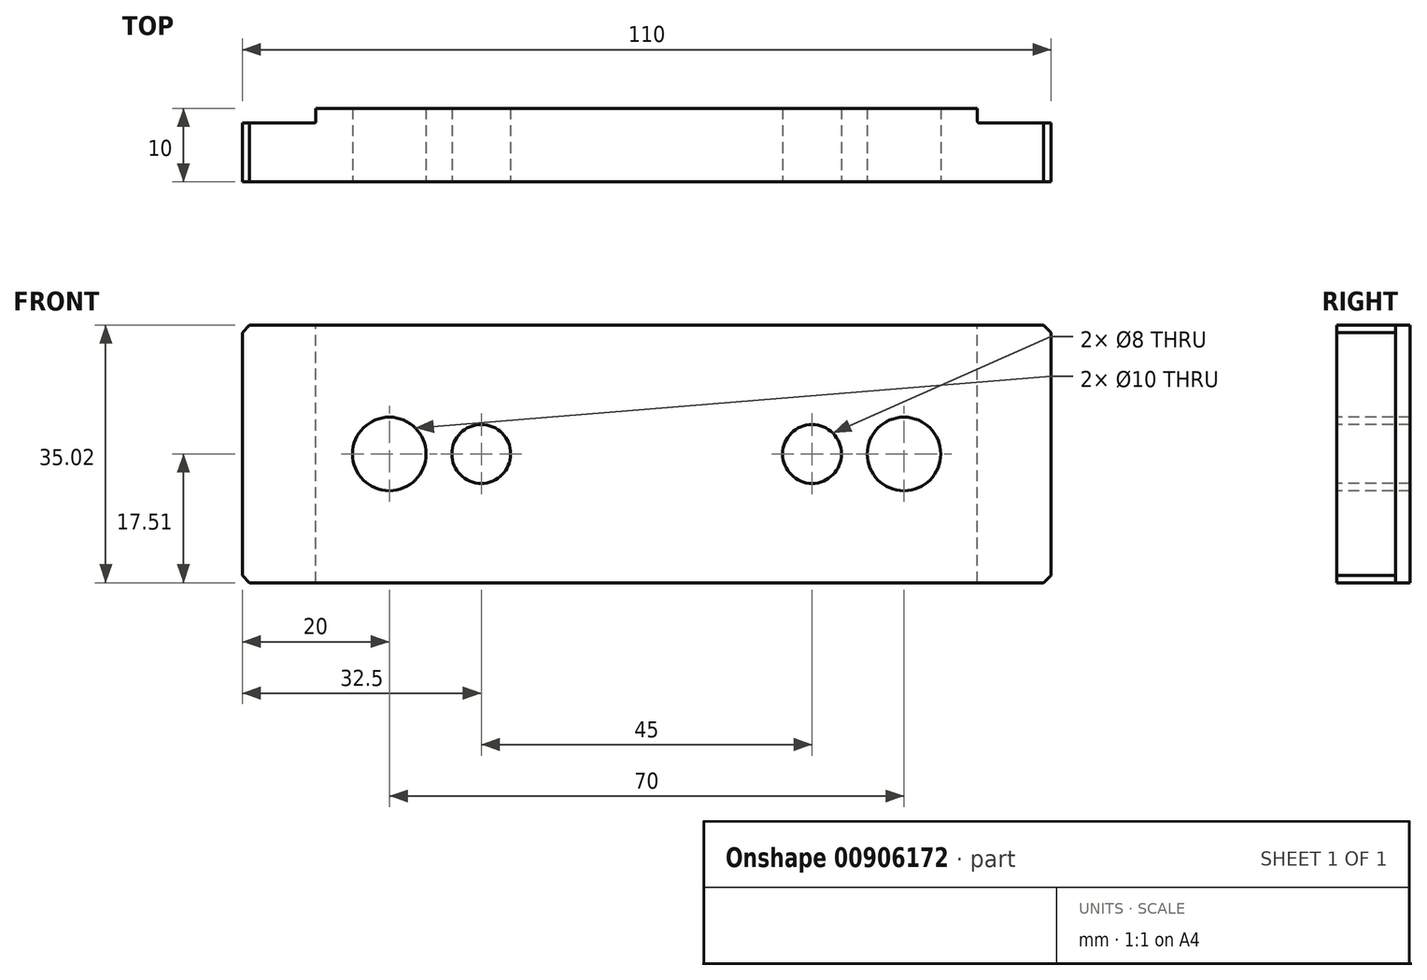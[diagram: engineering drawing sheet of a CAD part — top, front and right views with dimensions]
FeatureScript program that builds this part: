
annotation { "Feature Type Name" : "Feature", "Feature Type Description" : "" }
export const myFeature = defineFeature(function(context is Context, id is Id, definition is map)
    precondition{}
    {
        {
            var Q0;
            Q0=qCreatedBy(makeId("Front.planeOp"),FACE);
            var sketch = newSketch(context, id + "F0", { "sketchPlane" : qUnion([Q0])});
            skLineSegment(sketch, "E0.bottom", {"start": v(-55, -17.5) * mm, "end": v(55, -17.5) * mm});
            skLineSegment(sketch, "E0.top", {"start": v(-55, 17.5) * mm, "end": v(55, 17.5) * mm});
            skLineSegment(sketch, "E0.left", {"start": v(-55, -17.5) * mm, "end": v(-55, 17.5) * mm});
            skLineSegment(sketch, "E0.right", {"start": v(55, -17.5) * mm, "end": v(55, 17.5) * mm});
            skPoint(sketch, "E0.middle", {"position": v(0, 0) * mm});
            skCircle(sketch, "E1", {"center": v(-22.5, 0) * mm, "radius": 4 * mm});
            skCircle(sketch, "E2", {"center": v(22.5, 0) * mm, "radius": 4 * mm});
            skLineSegment(sketch, "E3", {"start": v(-22.5, 0) * mm, "end": v(0, 0) * mm});
            skLineSegment(sketch, "E4", {"start": v(22.5, 0) * mm, "end": v(0, 0) * mm});
            skCircle(sketch, "E5", {"center": v(-35, 0) * mm, "radius": 5 * mm});
            skCircle(sketch, "E6", {"center": v(35, 0) * mm, "radius": 5 * mm});
            skLineSegment(sketch, "E7", {"start": v(-35, 0) * mm, "end": v(0, 0) * mm});
            skLineSegment(sketch, "E8", {"start": v(35, 0) * mm, "end": v(0, 0) * mm});
            skLineSegment(sketch, "E9.bottom", {"start": v(-45, -17.5) * mm, "end": v(45, -17.5) * mm});
            skLineSegment(sketch, "E9.top", {"start": v(-45, 17.5) * mm, "end": v(45, 17.5) * mm});
            skLineSegment(sketch, "E9.left", {"start": v(-45, -17.5) * mm, "end": v(-45, 17.5) * mm});
            skLineSegment(sketch, "E9.right", {"start": v(45, -17.5) * mm, "end": v(45, 17.5) * mm});
            skSolve(sketch);
        }
        {
            var Q0;
            Q0 = qSketchRegion(id + "F0", true);
            extrude(context, id + "F1", {"entities" : qUnion([Q0]), "oppositeDirection" : true, "depth" : 8 * mm, "offsetDistance" : 25 * mm});
        }
        {
            var Q0;
            Q0=makeQuery(id+"F0.imprint","IMPRINT",FACE,{"disambiguationData":[TD([[makeQuery(id+"F0.imprint","IMPRINT",EDGE,{"derivedFrom":sQuery(id+"F0.wireOp",EDGE,"E5")}),-1.0]])]});
            extrude(context, id + "F2", {"entities" : qUnion([Q0]), "operationType" : NewBodyOperationType.ADD, "oppositeDirection" : true, "depth" : 10 * mm, "offsetDistance" : 25 * mm});
        }
        {
            var Q0;
            Q0=makeQuery(id+"F1.opExtrude","SWEPT_EDGE",EDGE,{"disambiguationData":[OSD([sQuery(id+"F0.wireOp",EDGE,"E0.bottom"),sQuery(id+"F0.wireOp",EDGE,"E0.right")])]});
            var Q1;
            Q1=makeQuery(id+"F1.opExtrude","SWEPT_EDGE",EDGE,{"disambiguationData":[OSD([sQuery(id+"F0.wireOp",EDGE,"E0.top"),sQuery(id+"F0.wireOp",EDGE,"E0.right")])]});
            var Q2;
            Q2=makeQuery(id+"F1.opExtrude","SWEPT_EDGE",EDGE,{"disambiguationData":[OSD([sQuery(id+"F0.wireOp",EDGE,"E0.bottom"),sQuery(id+"F0.wireOp",EDGE,"E0.left")])]});
            var Q3;
            Q3=makeQuery(id+"F1.opExtrude","SWEPT_EDGE",EDGE,{"disambiguationData":[OSD([sQuery(id+"F0.wireOp",EDGE,"E0.top"),sQuery(id+"F0.wireOp",EDGE,"E0.left")])]});
            chamfer(context, id + "F3", {"entities" : qUnion([Q0, Q1, Q2, Q3]), "width" : 1 * mm, "tangentPropagation" : true});
        }
        {
            var Q0;
            Q0=makeQuery(id+"F2.boolean.opBoolean","INTERSECT",EDGE,{"derivedFrom":[makeQuery(id+"F1.opExtrude","CAP_FACE",FACE,{"disambiguationData":[OSD([sQuery(id+"F0.wireOp",EDGE,"E0.bottom"),sQuery(id+"F0.wireOp",EDGE,"E0.top"),sQuery(id+"F0.wireOp",EDGE,"E0.left"),sQuery(id+"F0.wireOp",EDGE,"E0.right"),sQuery(id+"F0.wireOp",EDGE,"E1"),sQuery(id+"F0.wireOp",EDGE,"E2"),sQuery(id+"F0.wireOp",EDGE,"E5"),sQuery(id+"F0.wireOp",EDGE,"E6"),sQuery(id+"F0.wireOp",EDGE,"E9.bottom"),sQuery(id+"F0.wireOp",EDGE,"E9.top")])],"isStart":false}),makeQuery(id+"F2.opExtrude","SWEPT_FACE",FACE,{"disambiguationData":[OSD([sQuery(id+"F0.wireOp",EDGE,"E9.right")])]})]});
            var Q1;
            Q1=makeQuery(id+"F2.boolean.opBoolean","INTERSECT",EDGE,{"derivedFrom":[makeQuery(id+"F1.opExtrude","CAP_FACE",FACE,{"disambiguationData":[OSD([sQuery(id+"F0.wireOp",EDGE,"E0.bottom"),sQuery(id+"F0.wireOp",EDGE,"E0.top"),sQuery(id+"F0.wireOp",EDGE,"E0.left"),sQuery(id+"F0.wireOp",EDGE,"E0.right"),sQuery(id+"F0.wireOp",EDGE,"E1"),sQuery(id+"F0.wireOp",EDGE,"E2"),sQuery(id+"F0.wireOp",EDGE,"E5"),sQuery(id+"F0.wireOp",EDGE,"E6"),sQuery(id+"F0.wireOp",EDGE,"E9.bottom"),sQuery(id+"F0.wireOp",EDGE,"E9.top")])],"isStart":false}),makeQuery(id+"F2.opExtrude","SWEPT_FACE",FACE,{"disambiguationData":[OSD([sQuery(id+"F0.wireOp",EDGE,"E9.left")])]})]});
            fillet(context, id + "F4", {"entities" : qUnion([Q0, Q1]), "radius" : 0.2 * mm, "tangentPropagation" : true, "allowEdgeOverflow" : false});
        }
    });
